# Revit family: Door-Hardware_Electronic-Lock_Euro-Lock_3770
name_source: partatom
category: Generic Models
revit_build: Autodesk Revit 2016 (Build: 20150714_1515(x64)
units: mm (PartAtom-declared; Revit-internal decimal feet)

## family parameters
Always vertical = No
Can host rebar = No
Cut with Voids When Loaded = No
OmniClass Number = 23.30.40.11.34
OmniClass Title = Automatic Door Controls and Operators
Part Type = Normal
Room Calculation Point = No
Round Connector Dimension = Use Diameter
Shared = No
Work Plane-Based = Yes

## types (1)
- as Specified
    Assembly Code = E1090900
    Available Options = as Specified
    Battery Operated = Yes
    Capacity = as Specified
    Default Elevation = 0' - 0"
    Description = Euro-Lock Electronic Latch Lock - Model 3770
    Expected Lifespan (Years) = 0
    Hardware Operation = I-Button  ;  Proximity Card  ;  Keypad
    Installation Phase = Door Hardware
    Maintenance Schedule (Months) = 0
    Manufacturer = Euro-Locks, Inc
    Manufacturer Fax = 616-994-0480
    Manufacturer Website = http://www.lowe-and-fletcher.com
    Model = 3770
    Product Data = http://www.arcat.com
    Revision = R1_2015-09
    Sales Information = http://www.lowe-and-fletcher.com
    Standards Conformance = as Specified
    URL = http://www.lowe-and-fletcher.com
    Unit Depth = 0' - 1 1/16"
    Unit Height = 0' - 5 3/8"
    Unit Width = 0' - 1 15/32"
    Warranty Duration (Years) = 0

## geometry (parser evidence)
native form markers: Sweep x3
no freeform markers — native parametric forms only
